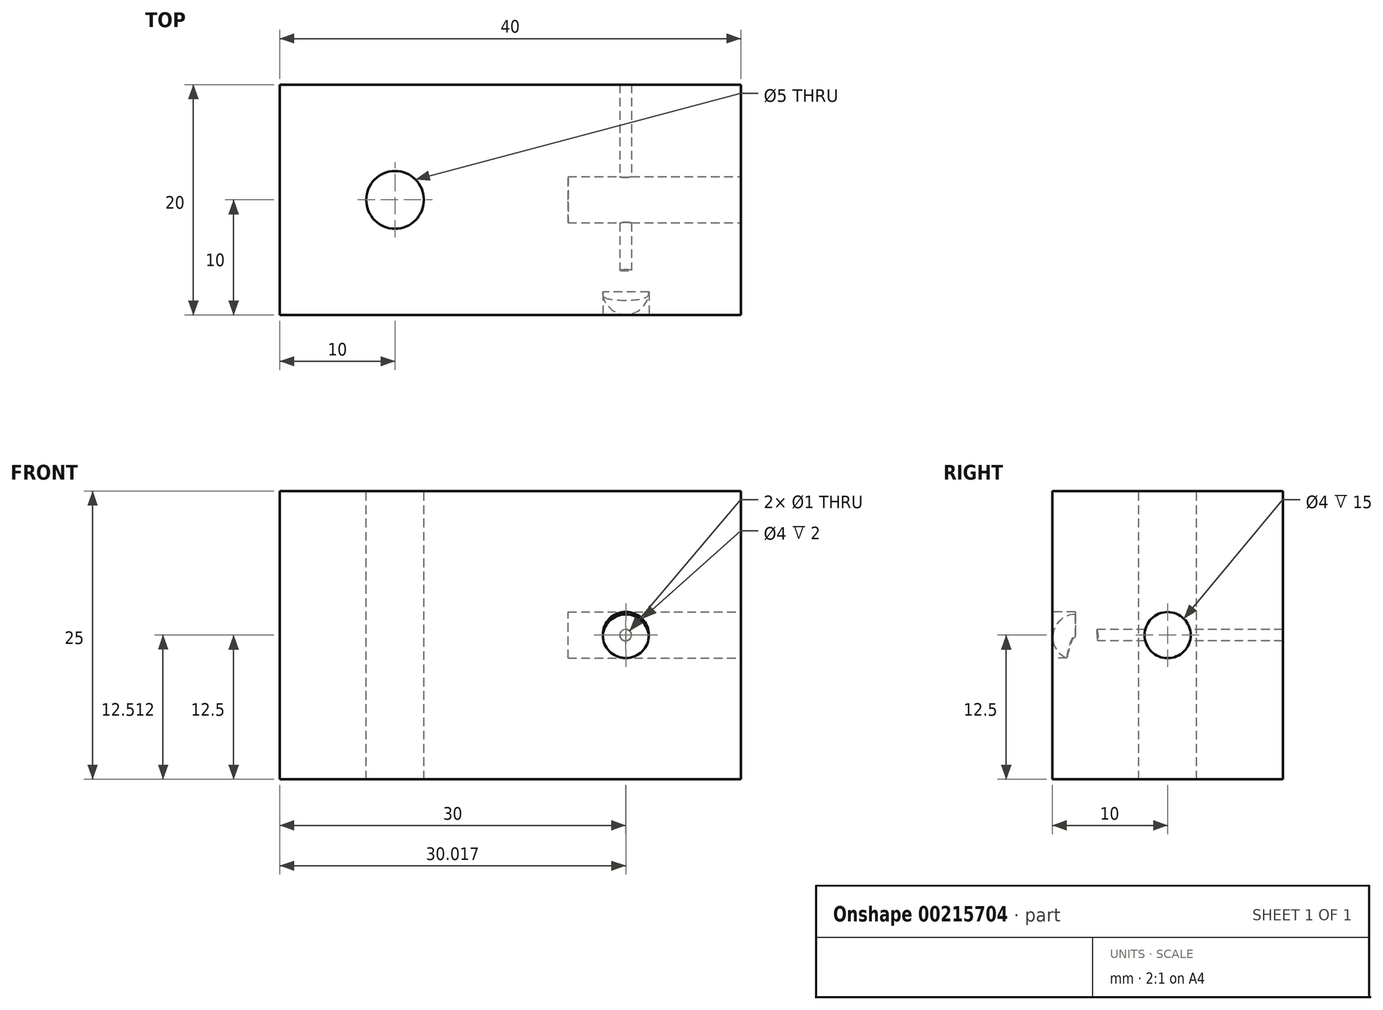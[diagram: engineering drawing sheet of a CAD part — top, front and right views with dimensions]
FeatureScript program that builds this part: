
annotation { "Feature Type Name" : "Feature", "Feature Type Description" : "" }
export const myFeature = defineFeature(function(context is Context, id is Id, definition is map)
    precondition{}
    {
        {
            var Q0;
            Q0=qCreatedBy(makeId("Front.planeOp"),FACE);
            var sketch = newSketch(context, id + "F0", { "sketchPlane" : qUnion([Q0])});
            skLineSegment(sketch, "E0.bottom", {"start": v(0, 0) * mm, "end": v(40, 0) * mm});
            skLineSegment(sketch, "E0.top", {"start": v(0, -25) * mm, "end": v(40, -25) * mm});
            skLineSegment(sketch, "E0.left", {"start": v(0, 0) * mm, "end": v(0, -25) * mm});
            skLineSegment(sketch, "E0.right", {"start": v(40, 0) * mm, "end": v(40, -25) * mm});
            skSolve(sketch);
        }
        {
            var Q0;
            Q0 = qSketchRegion(id + "F0", true);
            extrude(context, id + "F1", {"entities" : qUnion([Q0]), "oppositeDirection" : true, "depth" : 20 * mm});
        }
        {
            var Q0;
            Q0=makeQuery(id+"F1.opExtrude","SWEPT_FACE",FACE,{"disambiguationData":[OSD([sQuery(id+"F0.wireOp",EDGE,"E0.right")])]});
            var sketch = newSketch(context, id + "F2", { "sketchPlane" : qUnion([Q0])});
            skCircle(sketch, "E1", {"center": v(10, -12.5) * mm, "radius": 2 * mm});
            skSolve(sketch);
        }
        {
            var Q0;
            Q0 = qSketchRegion(id + "F2", true);
            extrude(context, id + "F3", {"entities" : qUnion([Q0]), "operationType" : NewBodyOperationType.REMOVE, "oppositeDirection" : true, "depth" : 15 * mm});
        }
        {
            var Q0;
            Q0=makeQuery(id+"F1.opExtrude","SWEPT_FACE",FACE,{"disambiguationData":[OSD([sQuery(id+"F0.wireOp",EDGE,"E0.bottom")])]});
            var sketch = newSketch(context, id + "F4", { "sketchPlane" : qUnion([Q0])});
            skCircle(sketch, "E2", {"center": v(10, 10) * mm, "radius": 2.5 * mm});
            skSolve(sketch);
        }
        {
            var Q0;
            Q0 = qSketchRegion(id + "F4", true);
            extrude(context, id + "F5", {"entities" : qUnion([Q0]), "operationType" : NewBodyOperationType.REMOVE, "endBound" : BoundingType.THROUGH_ALL, "oppositeDirection" : true, "depth" : 25 * mm});
        }
        {
            var Q0;
            Q0=makeQuery(id+"F1.opExtrude","CAP_FACE",FACE,{"disambiguationData":[OSD([sQuery(id+"F0.wireOp",EDGE,"E0.bottom"),sQuery(id+"F0.wireOp",EDGE,"E0.top"),sQuery(id+"F0.wireOp",EDGE,"E0.left"),sQuery(id+"F0.wireOp",EDGE,"E0.right")])],"isStart":true});
            var sketch = newSketch(context, id + "F6", { "sketchPlane" : qUnion([Q0])});
            skCircle(sketch, "E3", {"center": v(30, -12.5) * mm, "radius": 0.5 * mm});
            skSolve(sketch);
        }
        {
            var Q0;
            Q0 = qSketchRegion(id + "F6", true);
            extrude(context, id + "F7", {"entities" : qUnion([Q0]), "operationType" : NewBodyOperationType.REMOVE, "endBound" : BoundingType.THROUGH_ALL, "oppositeDirection" : true, "depth" : 25 * mm});
        }
        {
            var Q0;
            Q0=makeQuery(id+"F1.opExtrude","CAP_FACE",FACE,{"disambiguationData":[OSD([sQuery(id+"F0.wireOp",EDGE,"E0.bottom"),sQuery(id+"F0.wireOp",EDGE,"E0.top"),sQuery(id+"F0.wireOp",EDGE,"E0.left"),sQuery(id+"F0.wireOp",EDGE,"E0.right")])],"isStart":true});
            cPlane(context, id + "F8", {"entities" : qUnion([Q0]), "cplaneType" : CPlaneType.OFFSET, "offset" : 2 * mm, "oppositeDirection" : true, "width" : 150 * mm, "height" : 150 * mm});
        }
        {
            var Q0;
            Q0=qCreatedBy(id+"F8.planeOp",FACE);
            var sketch = newSketch(context, id + "F9", { "sketchPlane" : qUnion([Q0])});
            skArc(sketch, "E4", {"start": v(28, -12.68) * mm, "mid": v(30.03, -14.63) * mm, "end": v(32, -12.65) * mm});
            skLineSegment(sketch, "E5", {"start": v(28, -12.68) * mm, "end": v(32, -12.65) * mm});
            skSolve(sketch);
        }
        {
            var Q0;
            Q0 = qSketchRegion(id + "F9", true);
            var Q1;
            Q1=sQuery(id+"F9.wireOp",EDGE,"E5");
            revolve(context, id + "F10", {"operationType" : NewBodyOperationType.REMOVE, "entities" : qUnion([Q0]), "axis" : qUnion([Q1]), "revolveType" : RevolveType.FULL, "oppositeDirection" : true});
        }
        {
            var Q0;
            Q0=makeQuery(id+"F1.opExtrude","CAP_FACE",FACE,{"disambiguationData":[OSD([sQuery(id+"F0.wireOp",EDGE,"E0.bottom"),sQuery(id+"F0.wireOp",EDGE,"E0.top"),sQuery(id+"F0.wireOp",EDGE,"E0.left"),sQuery(id+"F0.wireOp",EDGE,"E0.right")])],"isStart":true});
            var sketch = newSketch(context, id + "F11", { "sketchPlane" : qUnion([Q0])});
            skCircle(sketch, "E6", {"center": v(30.02, -12.49) * mm, "radius": 2 * mm});
            skSolve(sketch);
        }
        {
            var Q0;
            Q0 = qSketchRegion(id + "F11", true);
            extrude(context, id + "F12", {"entities" : qUnion([Q0]), "operationType" : NewBodyOperationType.REMOVE, "oppositeDirection" : true, "depth" : 2 * mm});
        }
    });
